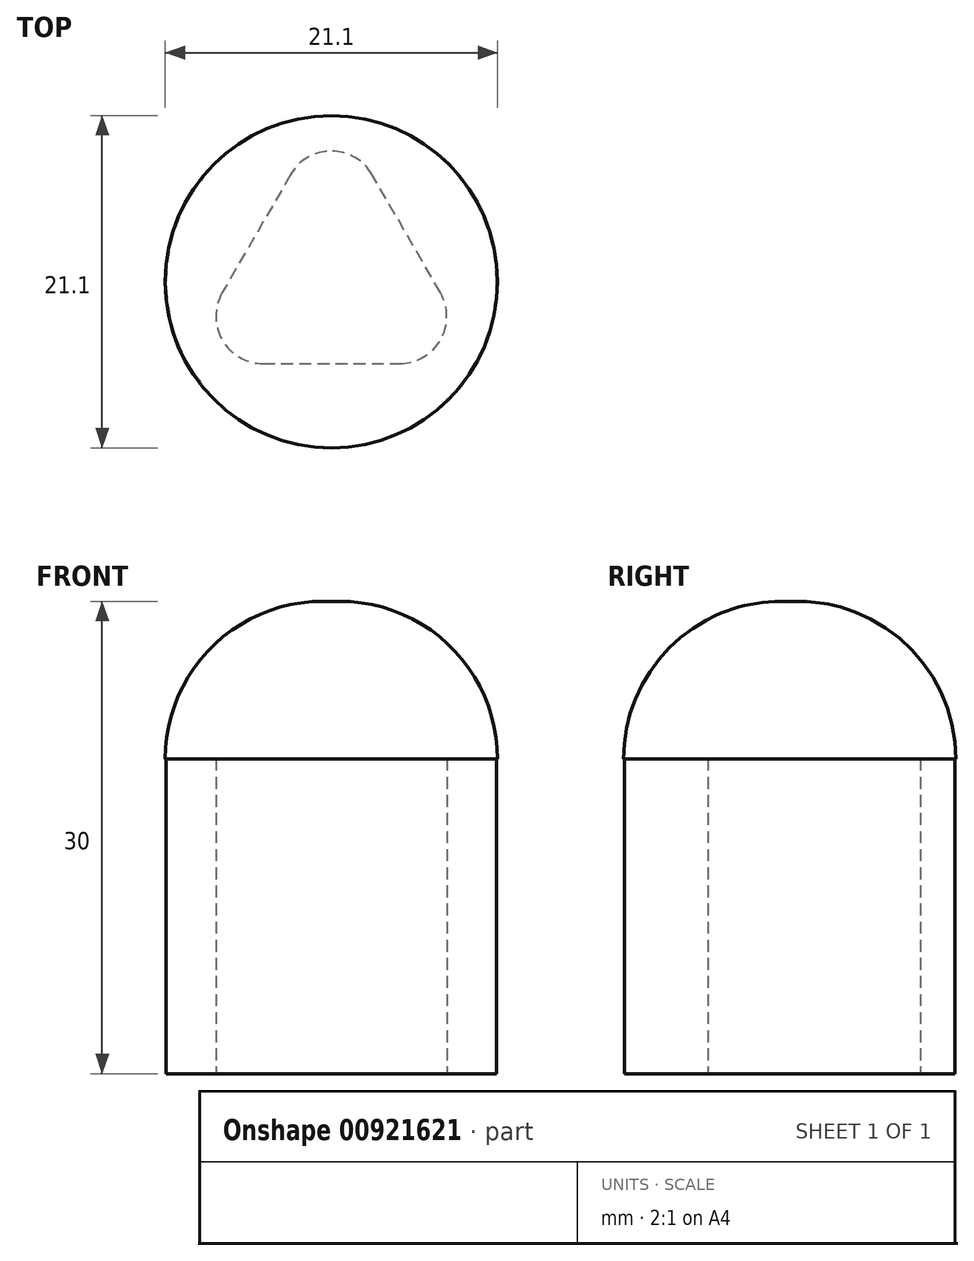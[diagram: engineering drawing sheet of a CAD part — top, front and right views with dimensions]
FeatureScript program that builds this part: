
annotation { "Feature Type Name" : "Feature", "Feature Type Description" : "" }
export const myFeature = defineFeature(function(context is Context, id is Id, definition is map)
    precondition{}
    {
        {
            var Q0;
            Q0=qCreatedBy(makeId("Top.planeOp"),FACE);
            var sketch = newSketch(context, id + "F0", { "sketchPlane" : qUnion([Q0])});
            skLineSegment(sketch, "E0", {"start": v(5.2, 0) * mm, "end": v(13.86, 0) * mm});
            skLineSegment(sketch, "E1", {"start": v(16.45, 4.5) * mm, "end": v(12.12, 12) * mm});
            skLineSegment(sketch, "E2", {"start": v(6.93, 12) * mm, "end": v(2.6, 4.5) * mm});
            skPoint(sketch, "E3.visualSharp", {"position": v(9.53, 16.5) * mm});
            skArc(sketch, "E3.filletArc", {"start": v(12.12, 12) * mm, "mid": v(9.53, 13.5) * mm, "end": v(6.93, 12) * mm});
            skPoint(sketch, "E4.visualSharp", {"position": v(19.05, 0) * mm});
            skArc(sketch, "E4.filletArc", {"start": v(13.86, 0) * mm, "mid": v(16.45, 1.5) * mm, "end": v(16.45, 4.5) * mm});
            skPoint(sketch, "E5.visualSharp", {"position": v(0, 0) * mm});
            skArc(sketch, "E5.filletArc", {"start": v(2.6, 4.5) * mm, "mid": v(2.6, 1.5) * mm, "end": v(5.2, 0) * mm});
            skCircle(sketch, "E6", {"center": v(9.53, 5.2) * mm, "radius": 10.5 * mm});
            skSolve(sketch);
        }
        {
            var Q0;
            Q0 = qSketchRegion(id + "F0", true);
            extrude(context, id + "F1", {"entities" : qUnion([Q0]), "depth" : 20 * mm, "offsetDistance" : 25 * mm});
        }
        {
            var Q0;
            Q0=qCreatedBy(makeId("Front.planeOp"),FACE);
            cPlane(context, id + "F2", {"entities" : qUnion([Q0]), "cplaneType" : CPlaneType.OFFSET, "offset" : 5.2 * mm, "oppositeDirection" : true, "width" : 150 * mm, "height" : 150 * mm});
        }
        {
            var Q0;
            Q0=qCreatedBy(id+"F2.planeOp",FACE);
            var sketch = newSketch(context, id + "F3", { "sketchPlane" : qUnion([Q0])});
            skLineSegment(sketch, "E7", {"start": v(9.53, 24.25) * mm, "end": v(9.53, 7.18) * mm, "construction": true});
            skLineSegment(sketch, "E8", {"start": v(9.53, 20) * mm, "end": v(9.53, 30) * mm});
            skLineSegment(sketch, "E9", {"start": v(9.53, 30) * mm, "end": v(10.08, 30) * mm});
            skArc(sketch, "E10", {"start": v(20.08, 20) * mm, "mid": v(17.15, 27.07) * mm, "end": v(10.08, 30) * mm});
            skLineSegment(sketch, "E11", {"start": v(20.08, 20) * mm, "end": v(9.53, 20) * mm});
            skSolve(sketch);
        }
        {
            var Q0;
            Q0=makeQuery(id+"F3.imprint","IMPRINT",FACE,{"disambiguationData":[TD([[makeQuery(id+"F3.imprint","IMPRINT",EDGE,{"derivedFrom":sQuery(id+"F3.wireOp",EDGE,"E8")}),-1.0]])]});
            var Q1;
            Q1=sQuery(id+"F3.wireOp",EDGE,"E7");
            revolve(context, id + "F4", {"operationType" : NewBodyOperationType.ADD, "surfaceOperationType" : NewSurfaceOperationType.NEW, "entities" : qUnion([Q0]), "axis" : qUnion([Q1]), "revolveType" : RevolveType.FULL});
        }
    });
